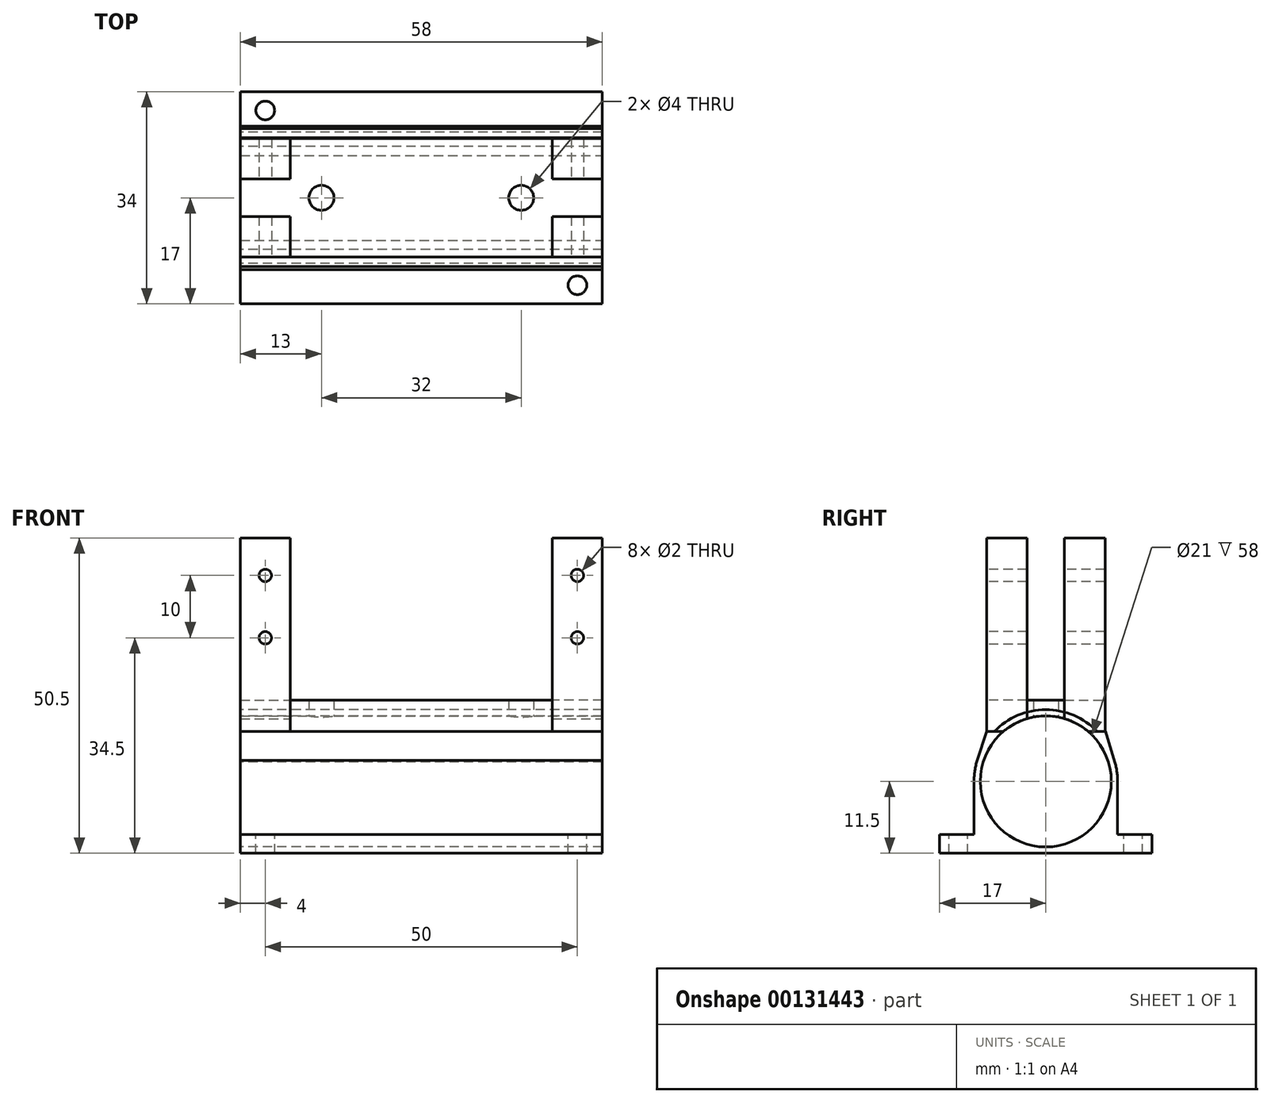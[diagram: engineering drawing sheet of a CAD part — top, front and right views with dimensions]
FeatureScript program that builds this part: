
annotation { "Feature Type Name" : "Feature", "Feature Type Description" : "" }
export const myFeature = defineFeature(function(context is Context, id is Id, definition is map)
    precondition{}
    {
        {
            var Q0;
            Q0=qCreatedBy(makeId("Top.planeOp"),FACE);
            var sketch = newSketch(context, id + "F0", { "sketchPlane" : qUnion([Q0])});
            skLineSegment(sketch, "E0.bottom", {"start": v(29, -9.5) * mm, "end": v(-29, -9.5) * mm});
            skLineSegment(sketch, "E0.top", {"start": v(29, 9.5) * mm, "end": v(-29, 9.5) * mm});
            skLineSegment(sketch, "E0.left", {"start": v(29, -9.5) * mm, "end": v(29, 9.5) * mm});
            skLineSegment(sketch, "E0.right", {"start": v(-29, -9.5) * mm, "end": v(-29, 9.5) * mm});
            skPoint(sketch, "E0.middle", {"position": v(0, 0) * mm});
            skCircle(sketch, "E1", {"center": v(16, 0) * mm, "radius": 2 * mm});
            skLineSegment(sketch, "E2", {"start": v(29, 3) * mm, "end": v(21, 3) * mm});
            skLineSegment(sketch, "E3", {"start": v(21, 3) * mm, "end": v(21, 9.5) * mm});
            skLineSegment(sketch, "E4.MirrorCS", {"start": v(21, -3) * mm, "end": v(21, -9.5) * mm});
            skLineSegment(sketch, "E5.MirrorCS", {"start": v(29, -3) * mm, "end": v(21, -3) * mm});
            skCircle(sketch, "E6.MirrorC", {"center": v(-16, 0) * mm, "radius": 2 * mm});
            skLineSegment(sketch, "E7.MirrorCS", {"start": v(-21, 3) * mm, "end": v(-21, 9.5) * mm});
            skLineSegment(sketch, "E8.MirrorCS", {"start": v(-29, 3) * mm, "end": v(-21, 3) * mm});
            skLineSegment(sketch, "E9.MirrorCS", {"start": v(-29, -3) * mm, "end": v(-21, -3) * mm});
            skLineSegment(sketch, "E10.MirrorCS", {"start": v(-21, -3) * mm, "end": v(-21, -9.5) * mm});
            skCircle(sketch, "E11", {"center": v(25, -14) * mm, "radius": 1.5 * mm});
            skCircle(sketch, "E12.MirrorC", {"center": v(25, 14) * mm, "radius": 1.5 * mm});
            skCircle(sketch, "E13.MirrorC", {"center": v(-25, 14) * mm, "radius": 1.5 * mm});
            skCircle(sketch, "E14.MirrorC", {"center": v(-25, -14) * mm, "radius": 1.5 * mm});
            skSolve(sketch);
        }
        {
            var Q0;
            {var subQ3=sQuery(id+"F0.wireOp",EDGE,"E7.MirrorCS");Q0=makeQuery(id+"F0.imprint","IMPRINT",FACE,{"disambiguationData":[TD([[makeQuery(id+"F0.imprint","IMPRINT",EDGE,{"derivedFrom":subQ3}),1.0]])]});}
            var Q1;
            {var subQ4=sQuery(id+"F0.wireOp",EDGE,"E9.MirrorCS");Q1=makeQuery(id+"F0.imprint","IMPRINT",FACE,{"disambiguationData":[TD([[makeQuery(id+"F0.imprint","IMPRINT",EDGE,{"derivedFrom":subQ4}),-1.0]])]});}
            var Q2;
            {var subQ4=sQuery(id+"F0.wireOp",EDGE,"E2");Q2=makeQuery(id+"F0.imprint","IMPRINT",FACE,{"disambiguationData":[TD([[makeQuery(id+"F0.imprint","IMPRINT",EDGE,{"derivedFrom":subQ4}),-1.0]])]});}
            var Q3;
            {var subQ3=sQuery(id+"F0.wireOp",EDGE,"E4.MirrorCS");Q3=makeQuery(id+"F0.imprint","IMPRINT",FACE,{"disambiguationData":[TD([[makeQuery(id+"F0.imprint","IMPRINT",EDGE,{"derivedFrom":subQ3}),1.0]])]});}
            extrude(context, id + "F1", {"entities" : qUnion([Q0, Q1, Q2, Q3]), "depth" : 31 * mm});
        }
        {
            var Q0;
            Q0=makeQuery(id+"F0.imprint","IMPRINT",FACE,{"disambiguationData":[TD([[makeQuery(id+"F0.imprint","IMPRINT",EDGE,{"derivedFrom":sQuery(id+"F0.wireOp",EDGE,"E1")}),-1.0]])]});
            extrude(context, id + "F2", {"entities" : qUnion([Q0]), "depth" : 5 * mm});
        }
        {
            var Q0;
            Q0=qCreatedBy(makeId("Front.planeOp"),FACE);
            var sketch = newSketch(context, id + "F3", { "sketchPlane" : qUnion([Q0])});
            skCircle(sketch, "E15", {"center": v(25, 25) * mm, "radius": 1 * mm});
            skCircle(sketch, "E16", {"center": v(25, 15) * mm, "radius": 1 * mm});
            skCircle(sketch, "E17.MirrorC", {"center": v(-25, 25) * mm, "radius": 1 * mm});
            skCircle(sketch, "E18.MirrorC", {"center": v(-25, 15) * mm, "radius": 1 * mm});
            skSolve(sketch);
        }
        {
            var Q0;
            Q0 = qSketchRegion(id + "F3", true);
            extrude(context, id + "F4", {"entities" : qUnion([Q0]), "operationType" : NewBodyOperationType.REMOVE, "endBound" : BoundingType.SYMMETRIC, "oppositeDirection" : true, "depth" : 25 * mm});
        }
        {
            var Q0;
            Q0=qCreatedBy(makeId("Right.planeOp"),FACE);
            var sketch = newSketch(context, id + "F5", { "sketchPlane" : qUnion([Q0])});
            skCircle(sketch, "E19", {"center": v(0, -8) * mm, "radius": 10.5 * mm});
            skCircle(sketch, "E20", {"center": v(0, -8) * mm, "radius": 11.5 * mm});
            skLineSegment(sketch, "E21", {"start": v(0, -19.5) * mm, "end": v(11.5, -19.5) * mm});
            skLineSegment(sketch, "E22", {"start": v(11.5, -19.5) * mm, "end": v(11.5, -8) * mm});
            skLineSegment(sketch, "E23", {"start": v(0, -19.5) * mm, "end": v(-11.5, -19.5) * mm});
            skLineSegment(sketch, "E24", {"start": v(-11.5, -19.5) * mm, "end": v(-11.5, -8) * mm});
            skLineSegment(sketch, "E25", {"start": v(-9.45, 0) * mm, "end": v(-10.99, -4.6) * mm});
            skLineSegment(sketch, "E26", {"start": v(9.6, 0) * mm, "end": v(11.07, -4.88) * mm});
            skLineSegment(sketch, "E27", {"start": v(0, -19.5) * mm, "end": v(17, -19.5) * mm});
            skPoint(sketch, "E27.endSnap0", {"position": v(5.75, -19.5) * mm});
            skLineSegment(sketch, "E28", {"start": v(17, -19.5) * mm, "end": v(-17, -19.5) * mm});
            skLineSegment(sketch, "E29", {"start": v(-17, -19.5) * mm, "end": v(-17, -16.5) * mm});
            skLineSegment(sketch, "E30", {"start": v(-17, -16.5) * mm, "end": v(-11.5, -16.5) * mm});
            skLineSegment(sketch, "E31.MirrorCS", {"start": v(17, -16.5) * mm, "end": v(11.5, -16.5) * mm});
            skLineSegment(sketch, "E32.MirrorCS", {"start": v(17, -19.5) * mm, "end": v(17, -16.5) * mm});
            skLineSegment(sketch, "E33", {"start": v(-9.45, 0) * mm, "end": v(9.6, 0) * mm});
            skLineSegment(sketch, "E34", {"start": v(-6.8, 0) * mm, "end": v(6.8, 0) * mm});
            skSolve(sketch);
        }
        {
            var Q0;
            {var subQ0=sQuery(id+"F5.wireOp",EDGE,"E25");Q0=makeQuery(id+"F5.imprint","IMPRINT",FACE,{"disambiguationData":[TD([[makeQuery(id+"F5.imprint","IMPRINT",EDGE,{"derivedFrom":subQ0}),1.0]])]});}
            var Q1;
            {var subQ0=sQuery(id+"F5.wireOp",EDGE,"E26");Q1=makeQuery(id+"F5.imprint","IMPRINT",FACE,{"disambiguationData":[TD([[makeQuery(id+"F5.imprint","IMPRINT",EDGE,{"derivedFrom":subQ0}),-1.0]])]});}
            var Q2;
            Q2=makeQuery(id+"F5.imprint","IMPRINT",FACE,{"disambiguationData":[TD([[makeQuery(id+"F5.imprint","IMPRINT",EDGE,{"derivedFrom":sQuery(id+"F5.wireOp",EDGE,"E19")}),-1.0]])]});
            var Q3;
            {var subQ0=sQuery(id+"F5.wireOp",EDGE,"E22");var subQ1=sQuery(id+"F5.wireOp",EDGE,"E20");var subQ2=makeQuery(id+"F5.imprint","INTERSECT",VERTEX,{"derivedFrom":[subQ1,subQ0]});Q3=makeQuery(id+"F5.imprint","IMPRINT",FACE,{"disambiguationData":[TD([[makeQuery(id+"F5.imprint","IMPRINT",EDGE,{"disambiguationData":[TD([[subQ2,1.0]])],"derivedFrom":subQ1}),-1.0]])]});}
            var Q4;
            {var subQ0=sQuery(id+"F5.wireOp",EDGE,"E24");var subQ1=sQuery(id+"F5.wireOp",EDGE,"E20");var subQ2=makeQuery(id+"F5.imprint","INTERSECT",VERTEX,{"derivedFrom":[subQ1,subQ0]});Q4=makeQuery(id+"F5.imprint","IMPRINT",FACE,{"disambiguationData":[TD([[makeQuery(id+"F5.imprint","IMPRINT",EDGE,{"disambiguationData":[TD([[subQ2,-1.0]])],"derivedFrom":subQ1}),-1.0]])]});}
            var Q5;
            {var subQ4=sQuery(id+"F5.wireOp",EDGE,"E29");Q5=makeQuery(id+"F5.imprint","IMPRINT",FACE,{"disambiguationData":[TD([[makeQuery(id+"F5.imprint","IMPRINT",EDGE,{"derivedFrom":subQ4}),-1.0]])]});}
            var Q6;
            {var subQ3=sQuery(id+"F5.wireOp",EDGE,"E31.MirrorCS");Q6=makeQuery(id+"F5.imprint","IMPRINT",FACE,{"disambiguationData":[TD([[makeQuery(id+"F5.imprint","IMPRINT",EDGE,{"derivedFrom":subQ3}),1.0]])]});}
            var Q7;
            {var subQ10=sQuery(id+"F5.wireOp",EDGE,"E33");var subQ11=sQuery(id+"F5.wireOp",EDGE,"E19");var subQ12=makeQuery(id+"F5.imprint","INTERSECT",VERTEX,{"disambiguationData":[OD(0.0)],"derivedFrom":[subQ11,subQ10]});Q7=makeQuery(id+"F5.imprint","IMPRINT",FACE,{"disambiguationData":[TD([[makeQuery(id+"F5.imprint","IMPRINT",EDGE,{"disambiguationData":[TD([[subQ12,-1.0]])],"derivedFrom":subQ11}),-1.0]])]});}
            extrude(context, id + "F6", {"entities" : qUnion([Q0, Q1, Q2, Q3, Q4, Q5, Q6, Q7]), "endBound" : BoundingType.SYMMETRIC, "depth" : 58 * mm});
        }
        {
            var Q0;
            Q0=sQuery(id+"F5.wireOp",EDGE,"E19");
            extrude(context, id + "F7", {"bodyType" : ToolBodyType.SURFACE, "surfaceEntities" : qUnion([Q0]), "depth" : 25 * mm});
        }
        {
            var Q0;
            Q0=makeQuery(id+"F2.opExtrude","SWEPT_FACE",FACE,{"disambiguationData":[OSD([sQuery(id+"F0.wireOp",EDGE,"E0.left")])]});
            cPlane(context, id + "F8", {"entities" : qUnion([Q0]), "cplaneType" : CPlaneType.OFFSET, "offset" : 25 * mm, "width" : 150 * mm, "height" : 150 * mm});
        }
        {
            var Q0;
            Q0=qCreatedBy(id+"F8.planeOp",FACE);
            var sketch = newSketch(context, id + "F9", { "sketchPlane" : qUnion([Q0])});
            skCircle(sketch, "E35", {"center": v(0, -8) * mm, "radius": 10.5 * mm});
            skSolve(sketch);
        }
        {
            var Q0;
            Q0 = qSketchRegion(id + "F9", true);
            extrude(context, id + "F10", {"entities" : qUnion([Q0]), "operationType" : NewBodyOperationType.REMOVE, "endBound" : BoundingType.THROUGH_ALL, "oppositeDirection" : true, "depth" : 25 * mm});
        }
        {
            var Q0;
            Q0=makeQuery(id+"F0.imprint","IMPRINT",FACE,{"disambiguationData":[TD([[makeQuery(id+"F0.imprint","IMPRINT",EDGE,{"derivedFrom":sQuery(id+"F0.wireOp",EDGE,"E14.MirrorC")}),-1.0]])]});
            var Q1;
            Q1=makeQuery(id+"F0.imprint","IMPRINT",FACE,{"disambiguationData":[TD([[makeQuery(id+"F0.imprint","IMPRINT",EDGE,{"derivedFrom":sQuery(id+"F0.wireOp",EDGE,"E11")}),1.0]])]});
            var Q2;
            Q2=makeQuery(id+"F0.imprint","IMPRINT",FACE,{"disambiguationData":[TD([[makeQuery(id+"F0.imprint","IMPRINT",EDGE,{"derivedFrom":sQuery(id+"F0.wireOp",EDGE,"E13.MirrorC")}),1.0]])]});
            var Q3;
            Q3=makeQuery(id+"F0.imprint","IMPRINT",FACE,{"disambiguationData":[TD([[makeQuery(id+"F0.imprint","IMPRINT",EDGE,{"derivedFrom":sQuery(id+"F0.wireOp",EDGE,"E12.MirrorC")}),-1.0]])]});
            extrude(context, id + "F11", {"entities" : qUnion([Q0, Q1, Q2, Q3]), "operationType" : NewBodyOperationType.REMOVE, "endBound" : BoundingType.THROUGH_ALL, "oppositeDirection" : true, "depth" : 25 * mm});
        }
    });
